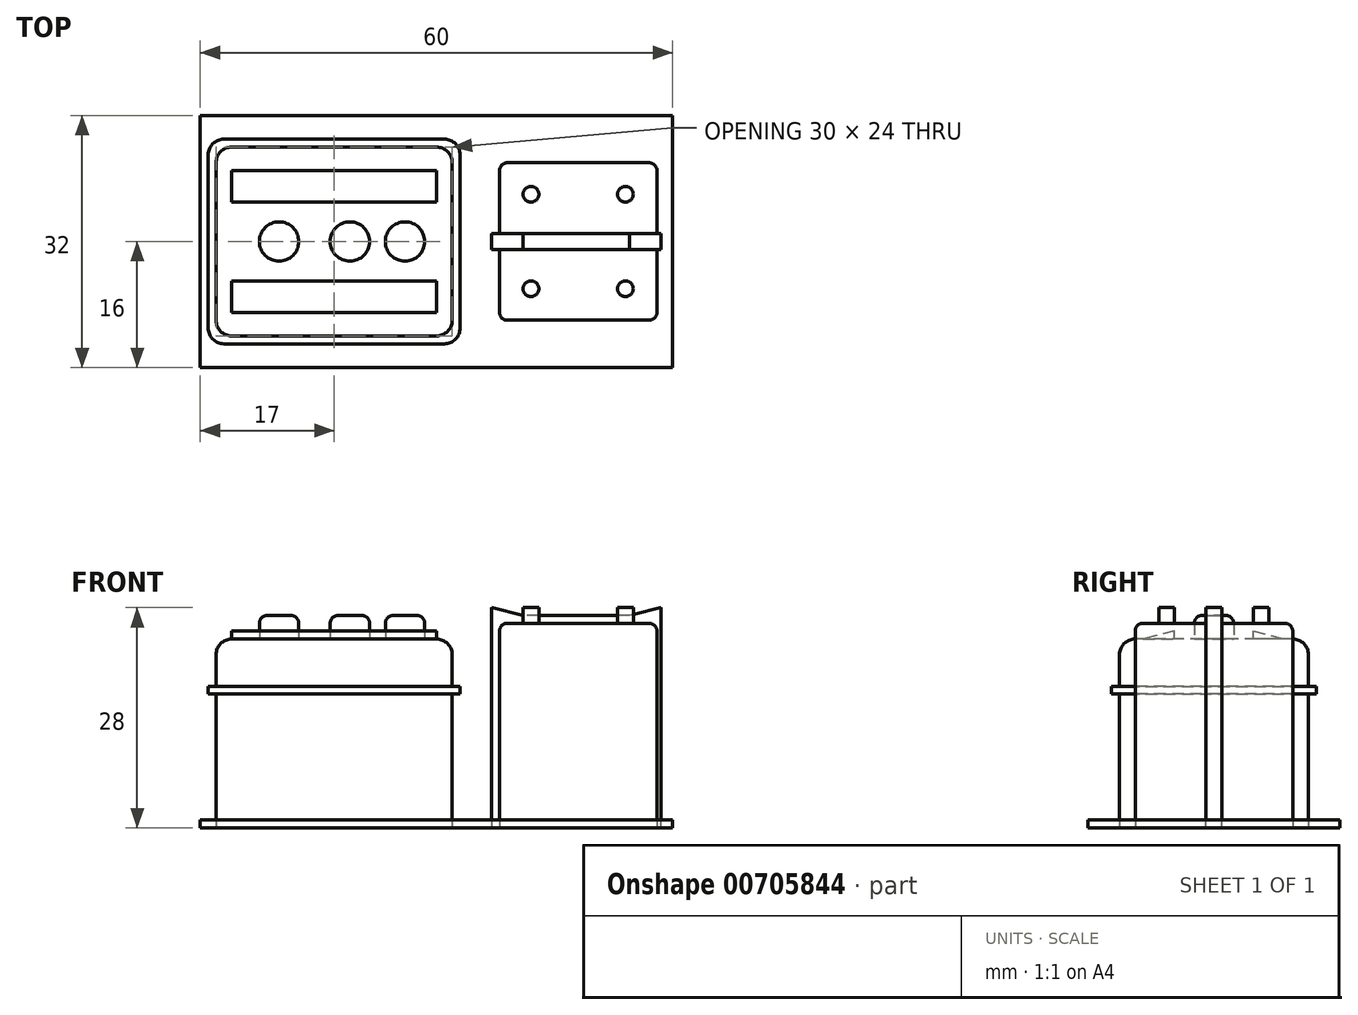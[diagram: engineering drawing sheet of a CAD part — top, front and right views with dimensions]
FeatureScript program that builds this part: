
annotation { "Feature Type Name" : "Feature", "Feature Type Description" : "" }
export const myFeature = defineFeature(function(context is Context, id is Id, definition is map)
    precondition{}
    {
        {
            var Q0;
            Q0=qCreatedBy(makeId("Right.planeOp"),FACE);
            cPlane(context, id + "F0", {"entities" : qUnion([Q0]), "cplaneType" : CPlaneType.OFFSET, "offset" : 2 * mm, "oppositeDirection" : true, "width" : 150 * mm, "height" : 150 * mm});
        }
        {
            var Q0;
            Q0=qCreatedBy(makeId("Top.planeOp"),FACE);
            var sketch = newSketch(context, id + "F1", { "sketchPlane" : qUnion([Q0])});
            skLineSegment(sketch, "E0.bottom", {"start": v(-30, 12) * mm, "end": v(0, 12) * mm});
            skLineSegment(sketch, "E0.top", {"start": v(-30, -12) * mm, "end": v(0, -12) * mm});
            skLineSegment(sketch, "E0.left", {"start": v(-30, 12) * mm, "end": v(-30, -12) * mm});
            skLineSegment(sketch, "E0.right", {"start": v(0, 12) * mm, "end": v(0, -12) * mm});
            skSolve(sketch);
        }
        {
            var Q0;
            Q0 = qSketchRegion(id + "F1", true);
            extrude(context, id + "F2", {"entities" : qUnion([Q0]), "depth" : 24 * mm, "offsetDistance" : 25 * mm});
        }
        {
            var Q0;
            Q0=makeQuery(id+"F2.opExtrude","SWEPT_EDGE",EDGE,{"disambiguationData":[OSD([sQuery(id+"F1.wireOp",EDGE,"E0.bottom"),sQuery(id+"F1.wireOp",EDGE,"E0.left")])]});
            var Q1;
            Q1=makeQuery(id+"F2.opExtrude","SWEPT_EDGE",EDGE,{"disambiguationData":[OSD([sQuery(id+"F1.wireOp",EDGE,"E0.bottom"),sQuery(id+"F1.wireOp",EDGE,"E0.right")])]});
            var Q2;
            Q2=makeQuery(id+"F2.opExtrude","SWEPT_EDGE",EDGE,{"disambiguationData":[OSD([sQuery(id+"F1.wireOp",EDGE,"E0.top"),sQuery(id+"F1.wireOp",EDGE,"E0.left")])]});
            var Q3;
            Q3=makeQuery(id+"F2.opExtrude","SWEPT_EDGE",EDGE,{"disambiguationData":[OSD([sQuery(id+"F1.wireOp",EDGE,"E0.top"),sQuery(id+"F1.wireOp",EDGE,"E0.right")])]});
            var Q4;
            Q4=makeQuery(id+"F2.opExtrude","CAP_FACE",FACE,{"disambiguationData":[OSD([sQuery(id+"F1.wireOp",EDGE,"E0.bottom"),sQuery(id+"F1.wireOp",EDGE,"E0.top"),sQuery(id+"F1.wireOp",EDGE,"E0.left"),sQuery(id+"F1.wireOp",EDGE,"E0.right")])],"isStart":false});
            fillet(context, id + "F3", {"entities" : qUnion([Q0, Q1, Q2, Q3, Q4]), "radius" : 2 * mm, "tangentPropagation" : true, "allowEdgeOverflow" : false});
        }
        {
            var Q0;
            Q0=qCreatedBy(makeId("Front.planeOp"),FACE);
            var sketch = newSketch(context, id + "F4", { "sketchPlane" : qUnion([Q0])});
            skLineSegment(sketch, "E1.bottom", {"start": v(-31, 18) * mm, "end": v(1, 18) * mm});
            skLineSegment(sketch, "E1.top", {"start": v(-31, 17) * mm, "end": v(1, 17) * mm});
            skLineSegment(sketch, "E1.left", {"start": v(-31, 18) * mm, "end": v(-31, 17) * mm});
            skLineSegment(sketch, "E1.right", {"start": v(1, 18) * mm, "end": v(1, 17) * mm});
            skSolve(sketch);
        }
        {
            var Q0;
            Q0 = qSketchRegion(id + "F4", true);
            extrude(context, id + "F5", {"entities" : qUnion([Q0]), "operationType" : NewBodyOperationType.ADD, "endBound" : BoundingType.SYMMETRIC, "depth" : 26 * mm, "offsetDistance" : 25 * mm});
        }
        {
            var Q0;
            Q0=makeQuery(id+"F5.opExtrude","CAP_EDGE",EDGE,{"disambiguationData":[OSD([sQuery(id+"F4.wireOp",EDGE,"E1.left")])],"isStart":true});
            var Q1;
            Q1=makeQuery(id+"F5.opExtrude","CAP_EDGE",EDGE,{"disambiguationData":[OSD([sQuery(id+"F4.wireOp",EDGE,"E1.left")])],"isStart":false});
            var Q2;
            Q2=makeQuery(id+"F5.opExtrude","CAP_EDGE",EDGE,{"disambiguationData":[OSD([sQuery(id+"F4.wireOp",EDGE,"E1.right")])],"isStart":true});
            var Q3;
            Q3=makeQuery(id+"F5.opExtrude","CAP_EDGE",EDGE,{"disambiguationData":[OSD([sQuery(id+"F4.wireOp",EDGE,"E1.right")])],"isStart":false});
            fillet(context, id + "F6", {"entities" : qUnion([Q0, Q1, Q2, Q3]), "radius" : 2 * mm, "tangentPropagation" : true, "allowEdgeOverflow" : false});
        }
        {
            var Q0;
            Q0=makeQuery(id+"F2.opExtrude","CAP_FACE",FACE,{"disambiguationData":[OSD([sQuery(id+"F1.wireOp",EDGE,"E0.bottom"),sQuery(id+"F1.wireOp",EDGE,"E0.top"),sQuery(id+"F1.wireOp",EDGE,"E0.left"),sQuery(id+"F1.wireOp",EDGE,"E0.right")])],"isStart":false});
            var sketch = newSketch(context, id + "F7", { "sketchPlane" : qUnion([Q0])});
            skCircle(sketch, "E2", {"center": v(-22, 0) * mm, "radius": 2.5 * mm});
            skCircle(sketch, "E3", {"center": v(-13, 0) * mm, "radius": 2.5 * mm});
            skCircle(sketch, "E4", {"center": v(-6, 0) * mm, "radius": 2.5 * mm});
            skSolve(sketch);
        }
        {
            var Q0;
            Q0 = qSketchRegion(id + "F7", true);
            extrude(context, id + "F8", {"entities" : qUnion([Q0]), "operationType" : NewBodyOperationType.ADD, "depth" : 3 * mm, "offsetDistance" : 25 * mm});
        }
        {
            var Q0;
            Q0=makeQuery(id+"F8.opExtrude","CAP_EDGE",EDGE,{"disambiguationData":[OSD([sQuery(id+"F7.wireOp",EDGE,"E2")])],"isStart":false});
            var Q1;
            Q1=makeQuery(id+"F8.opExtrude","CAP_EDGE",EDGE,{"disambiguationData":[OSD([sQuery(id+"F7.wireOp",EDGE,"E3")])],"isStart":false});
            var Q2;
            Q2=makeQuery(id+"F8.opExtrude","CAP_EDGE",EDGE,{"disambiguationData":[OSD([sQuery(id+"F7.wireOp",EDGE,"E4")])],"isStart":false});
            fillet(context, id + "F9", {"entities" : qUnion([Q0, Q1, Q2]), "radius" : 1 * mm, "tangentPropagation" : true, "allowEdgeOverflow" : false});
        }
        {
            var Q0;
            Q0=qCreatedBy(id+"F0.planeOp",FACE);
            var sketch = newSketch(context, id + "F10", { "sketchPlane" : qUnion([Q0])});
            skLineSegment(sketch, "E5", {"start": v(-5, 24) * mm, "end": v(-5, 25) * mm});
            skLineSegment(sketch, "E6", {"start": v(-5, 25) * mm, "end": v(-9, 24) * mm});
            skLineSegment(sketch, "E7", {"start": v(-9, 24) * mm, "end": v(-5, 24) * mm});
            skSolve(sketch);
        }
        {
            var Q0;
            Q0 = qSketchRegion(id + "F10", true);
            extrude(context, id + "F11", {"entities" : qUnion([Q0]), "oppositeDirection" : true, "depth" : 26 * mm, "offsetDistance" : 25 * mm});
        }
        {
            var Q0;
            Q0=makeQuery(id+"F11.opExtrude","SWEPT_BODY",BODY,{"disambiguationData":[OSD([sQuery(id+"F10.wireOp",EDGE,"E5"),sQuery(id+"F10.wireOp",EDGE,"E6"),sQuery(id+"F10.wireOp",EDGE,"E7")])]});
            var Q1;
            Q1=qCreatedBy(makeId("Front.planeOp"),FACE);
            mirror(context, id + "F12", {"entities" : qUnion([Q0]), "mirrorPlane" : qUnion([Q1])});
        }
        {
            var Q0;
            Q0=qCreatedBy(makeId("Top.planeOp"),FACE);
            var sketch = newSketch(context, id + "F13", { "sketchPlane" : qUnion([Q0])});
            skLineSegment(sketch, "E8.bottom", {"start": v(6, 10) * mm, "end": v(26, 10) * mm});
            skLineSegment(sketch, "E8.top", {"start": v(6, -10) * mm, "end": v(26, -10) * mm});
            skLineSegment(sketch, "E8.left", {"start": v(6, 10) * mm, "end": v(6, -10) * mm});
            skLineSegment(sketch, "E8.right", {"start": v(26, 10) * mm, "end": v(26, -10) * mm});
            skSolve(sketch);
        }
        {
            var Q0;
            Q0 = qSketchRegion(id + "F13", true);
            extrude(context, id + "F14", {"entities" : qUnion([Q0]), "depth" : 26 * mm, "offsetDistance" : 25 * mm});
        }
        {
            var Q0;
            Q0=makeQuery(id+"F14.opExtrude","SWEPT_EDGE",EDGE,{"disambiguationData":[OSD([sQuery(id+"F13.wireOp",EDGE,"E8.bottom"),sQuery(id+"F13.wireOp",EDGE,"E8.right")])]});
            var Q1;
            Q1=makeQuery(id+"F14.opExtrude","CAP_FACE",FACE,{"disambiguationData":[OSD([sQuery(id+"F13.wireOp",EDGE,"E8.bottom"),sQuery(id+"F13.wireOp",EDGE,"E8.top"),sQuery(id+"F13.wireOp",EDGE,"E8.left"),sQuery(id+"F13.wireOp",EDGE,"E8.right")])],"isStart":false});
            var Q2;
            Q2=makeQuery(id+"F14.opExtrude","SWEPT_EDGE",EDGE,{"disambiguationData":[OSD([sQuery(id+"F13.wireOp",EDGE,"E8.top"),sQuery(id+"F13.wireOp",EDGE,"E8.right")])]});
            var Q3;
            Q3=makeQuery(id+"F14.opExtrude","SWEPT_EDGE",EDGE,{"disambiguationData":[OSD([sQuery(id+"F13.wireOp",EDGE,"E8.bottom"),sQuery(id+"F13.wireOp",EDGE,"E8.left")])]});
            var Q4;
            Q4=makeQuery(id+"F14.opExtrude","SWEPT_EDGE",EDGE,{"disambiguationData":[OSD([sQuery(id+"F13.wireOp",EDGE,"E8.top"),sQuery(id+"F13.wireOp",EDGE,"E8.left")])]});
            fillet(context, id + "F15", {"entities" : qUnion([Q0, Q1, Q2, Q3, Q4]), "radius" : 1 * mm, "tangentPropagation" : true, "allowEdgeOverflow" : false});
        }
        {
            var Q0;
            Q0=makeQuery(id+"F14.opExtrude","CAP_FACE",FACE,{"disambiguationData":[OSD([sQuery(id+"F13.wireOp",EDGE,"E8.bottom"),sQuery(id+"F13.wireOp",EDGE,"E8.top"),sQuery(id+"F13.wireOp",EDGE,"E8.left"),sQuery(id+"F13.wireOp",EDGE,"E8.right")])],"isStart":false});
            var sketch = newSketch(context, id + "F16", { "sketchPlane" : qUnion([Q0])});
            skCircle(sketch, "E9", {"center": v(10, 6) * mm, "radius": 1 * mm});
            skCircle(sketch, "E10", {"center": v(22, 6) * mm, "radius": 1 * mm});
            skCircle(sketch, "E11", {"center": v(10, -6) * mm, "radius": 1 * mm});
            skCircle(sketch, "E12", {"center": v(22, -6) * mm, "radius": 1 * mm});
            skSolve(sketch);
        }
        {
            var Q0;
            Q0 = qSketchRegion(id + "F16", true);
            extrude(context, id + "F17", {"entities" : qUnion([Q0]), "operationType" : NewBodyOperationType.ADD, "depth" : 2 * mm, "offsetDistance" : 25 * mm});
        }
        {
            var Q0;
            Q0=qCreatedBy(makeId("Front.planeOp"),FACE);
            var sketch = newSketch(context, id + "F18", { "sketchPlane" : qUnion([Q0])});
            skLineSegment(sketch, "E13", {"start": v(5, 0) * mm, "end": v(26.5, 0) * mm});
            skLineSegment(sketch, "E14", {"start": v(26.5, 0) * mm, "end": v(26.5, 28) * mm});
            skLineSegment(sketch, "E15", {"start": v(26.5, 28) * mm, "end": v(22.5, 27) * mm});
            skLineSegment(sketch, "E16", {"start": v(22.5, 27) * mm, "end": v(9, 27) * mm});
            skLineSegment(sketch, "E17", {"start": v(9, 27) * mm, "end": v(5, 28) * mm});
            skLineSegment(sketch, "E18", {"start": v(5, 28) * mm, "end": v(5, 0) * mm});
            skSolve(sketch);
        }
        {
            var Q0;
            Q0 = qSketchRegion(id + "F18", true);
            extrude(context, id + "F19", {"entities" : qUnion([Q0]), "operationType" : NewBodyOperationType.ADD, "endBound" : BoundingType.SYMMETRIC, "depth" : 2 * mm, "offsetDistance" : 25 * mm});
        }
        {
            var Q0;
            Q0=qCreatedBy(makeId("Top.planeOp"),FACE);
            var sketch = newSketch(context, id + "F20", { "sketchPlane" : qUnion([Q0])});
            skLineSegment(sketch, "E19.bottom", {"start": v(-32, 16) * mm, "end": v(28, 16) * mm});
            skLineSegment(sketch, "E19.top", {"start": v(-32, -16) * mm, "end": v(28, -16) * mm});
            skLineSegment(sketch, "E19.left", {"start": v(-32, 16) * mm, "end": v(-32, -16) * mm});
            skLineSegment(sketch, "E19.right", {"start": v(28, 16) * mm, "end": v(28, -16) * mm});
            skSolve(sketch);
        }
        {
            var Q0;
            Q0 = qSketchRegion(id + "F20", true);
            extrude(context, id + "F21", {"entities" : qUnion([Q0]), "depth" : 1 * mm, "offsetDistance" : 25 * mm});
        }
    });
